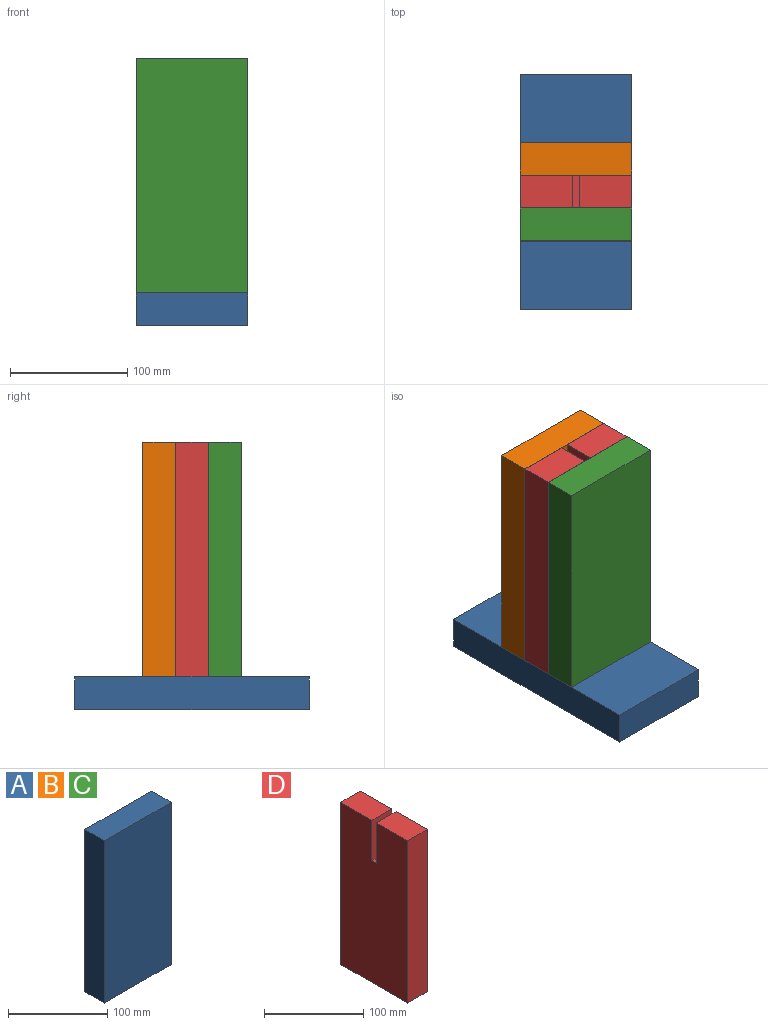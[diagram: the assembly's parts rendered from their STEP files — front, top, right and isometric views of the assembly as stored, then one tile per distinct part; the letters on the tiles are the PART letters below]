
ASSEMBLY  parts=4 mates=3
PART A: 6 faces, bbox 95x28x200 mm
  f0: plane 95x28mm, normal (0,0,-1), area 2660mm2, adj f1,f3,f4,f5
  f1: plane 200x28mm, normal (1,0,0), area 5600mm2, adj f0,f2,f4,f5
  f2: plane 95x28mm, normal (0,0,1), area 2660mm2, adj f1,f3,f4,f5
  f3: plane 200x28mm, normal (-1,0,0), area 5600mm2, adj f0,f2,f4,f5
  f4: plane 200x95mm, normal (0,-1,0), area 19000mm2, adj f0,f1,f2,f3
  f5: plane 200x95mm, normal (0,1,0), area 19000mm2, adj f0,f1,f2,f3
PART B: same geometry as A
PART C: same geometry as A
PART D: 10 faces, bbox 28x95x200 mm
  f0: plane 95x28mm, normal (0,0,-1), area 2660mm2, adj f1,f7,f8,f9
  f1: plane 200x28mm, normal (0,1,0), area 5600mm2, adj f0,f2,f8,f9
  f2: plane 44.3x28mm, normal (0,0,1), area 1240.4mm2, adj f1,f3,f8,f9
  f3: plane 50x28mm, normal (0,-1,0), area 1400mm2, adj f2,f4,f8,f9
  f4: plane 28x6.4mm, normal (0,0,1), area 179.2mm2, adj f3,f5,f8,f9
  f5: plane 50x28mm, normal (0,1,0), area 1400mm2, adj f4,f6,f8,f9
  f6: plane 44.3x28mm, normal (0,0,1), area 1240.4mm2, adj f5,f7,f8,f9
  f7: plane 200x28mm, normal (0,-1,0), area 5600mm2, adj f0,f6,f8,f9
  f8: plane 200x95mm, normal (1,0,0), area 18680mm2, adj f0,f1,f2,f3,f4,f5,f6,f7
  f9: plane 200x95mm, normal (-1,0,0), area 18680mm2, adj f0,f1,f2,f3,f4,f5,f6,f7
PLACE A rot(axis=(-1,0,0),90deg) t=(-91.51,-25.09,-220.51)mm
PLACE B t=(-91.51,16.91,-92.51)mm
PLACE C rot(axis=(1,0,0),180deg) t=(-91.51,-67.09,-92.51)mm
PLACE D rot(axis=(0,0,-1),90deg) t=(-91.51,-11.09,-92.51)mm
MATE fastened D.f9 <-> B.f4  axis (0,1,0) through (-91.51,-11.09,-192.51)mm
MATE fastened D.f0 <-> A.f4  axis (0,0,-1) through (-91.51,-25.09,-192.51)mm
MATE fastened D.f8 <-> C.f4  axis (0,-1,0) through (-91.51,-39.09,-192.51)mm
